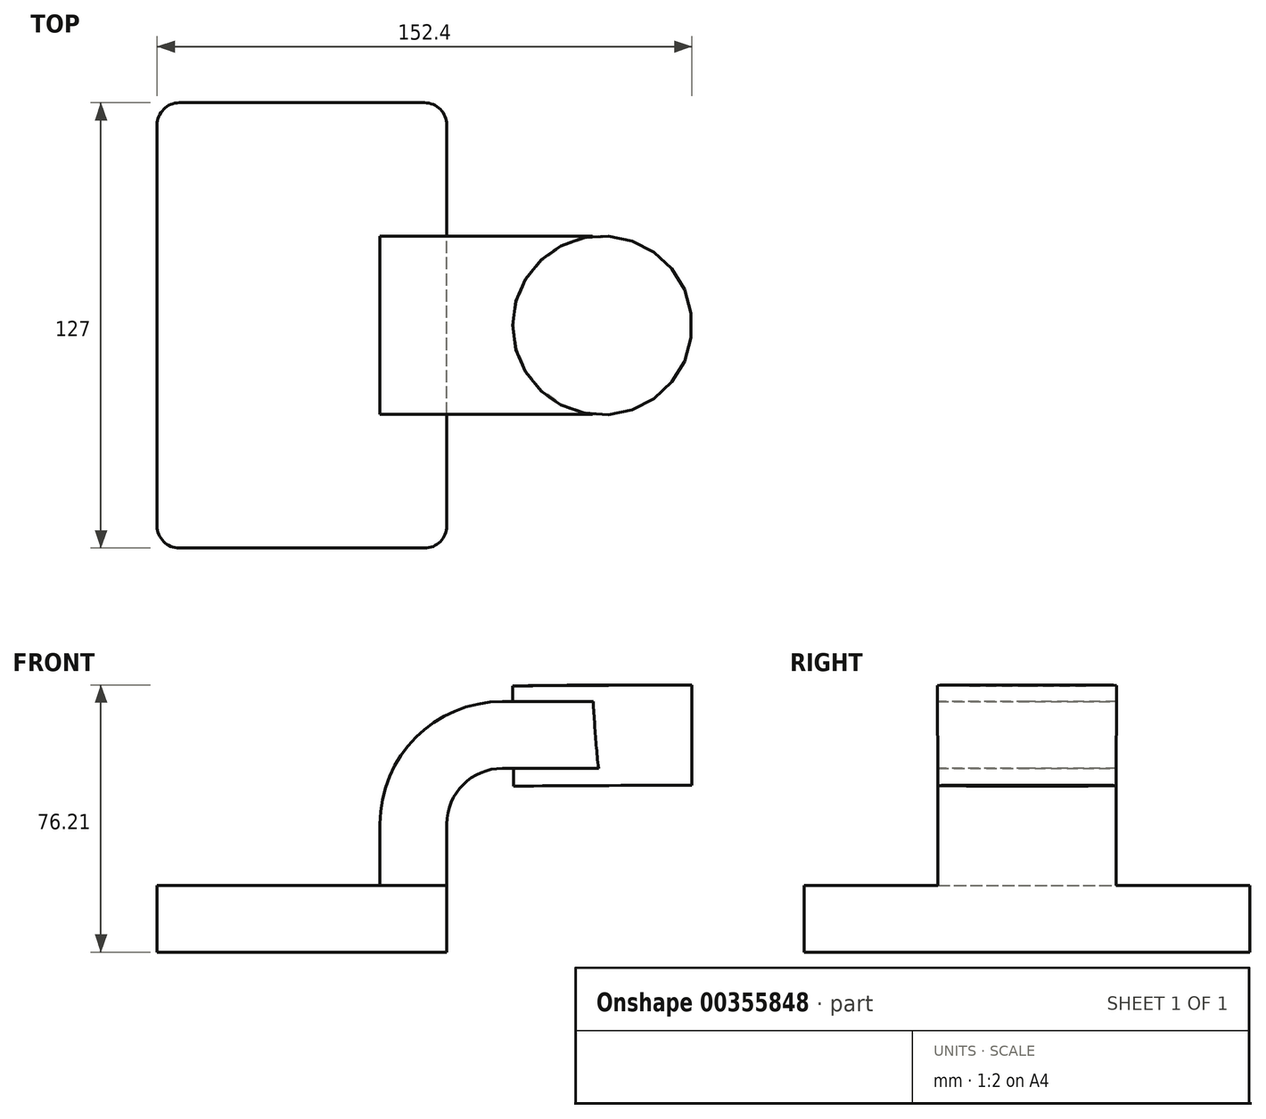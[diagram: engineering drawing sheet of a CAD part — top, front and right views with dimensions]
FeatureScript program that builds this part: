
annotation { "Feature Type Name" : "Feature", "Feature Type Description" : "" }
export const myFeature = defineFeature(function(context is Context, id is Id, definition is map)
    precondition{}
    {
        {
            var Q0;
            Q0=qCreatedBy(makeId("Front.planeOp"),FACE);
            var sketch = newSketch(context, id + "F0", { "sketchPlane" : qUnion([Q0])});
            skLineSegment(sketch, "E0.bottom", {"start": v(41.28, -9.52) * mm, "end": v(-41.28, -9.53) * mm});
            skLineSegment(sketch, "E0.top", {"start": v(41.28, 9.53) * mm, "end": v(-41.28, 9.53) * mm});
            skLineSegment(sketch, "E0.left", {"start": v(41.28, -9.52) * mm, "end": v(41.28, 9.53) * mm});
            skLineSegment(sketch, "E0.right", {"start": v(-41.28, -9.53) * mm, "end": v(-41.28, 9.53) * mm});
            skPoint(sketch, "E0.middle", {"position": v(0, 0) * mm});
            skLineSegment(sketch, "E1.bottom", {"start": v(111.12, 38.1) * mm, "end": v(60.32, 38.1) * mm});
            skLineSegment(sketch, "E1.top", {"start": v(111.12, 66.68) * mm, "end": v(60.32, 66.68) * mm});
            skLineSegment(sketch, "E1.left", {"start": v(111.12, 38.1) * mm, "end": v(111.12, 66.68) * mm});
            skLineSegment(sketch, "E1.right", {"start": v(60.32, 38.1) * mm, "end": v(60.32, 66.68) * mm});
            skPoint(sketch, "E1.middle", {"position": v(85.72, 52.39) * mm});
            skLineSegment(sketch, "E2", {"start": v(41.28, 9.53) * mm, "end": v(41.28, 27) * mm});
            skArc(sketch, "E3", {"start": v(41.27, 27) * mm, "mid": v(45.92, 38.23) * mm, "end": v(57.15, 42.88) * mm});
            skLineSegment(sketch, "E4", {"start": v(57.15, 42.88) * mm, "end": v(85.56, 42.88) * mm});
            skLineSegment(sketch, "E5.0", {"start": v(57.15, 61.93) * mm, "end": v(85.56, 61.93) * mm});
            skArc(sketch, "E5.1", {"start": v(22.23, 27) * mm, "mid": v(32.45, 51.7) * mm, "end": v(57.15, 61.93) * mm});
            skLineSegment(sketch, "E5.2", {"start": v(22.22, 9.53) * mm, "end": v(22.22, 27) * mm});
            skFitSpline(sketch, "E6", {"points": [v(-41.28, 9.52) * mm, v(57.15, 61.93) * mm], "startDerivative": vector(-2.62, 67.1) * mm, "endDerivative": vector(206.07, -1.73) * mm});
            skLineSegment(sketch, "E7", {"start": v(85.72, 38.1) * mm, "end": v(85.56, 66.68) * mm});
            skLineSegment(sketch, "E8", {"start": v(85.56, 61.93) * mm, "end": v(85.56, 42.88) * mm});
            skSolve(sketch);
        }
        {
            var Q0;
            Q0=makeQuery(id+"F0.imprint","IMPRINT",FACE,{"disambiguationData":[TD([[makeQuery(id+"F0.imprint","IMPRINT",EDGE,{"derivedFrom":sQuery(id+"F0.wireOp",EDGE,"E0.bottom")}),-1.0]])]});
            extrude(context, id + "F1", {"entities" : qUnion([Q0]), "endBound" : BoundingType.SYMMETRIC, "depth" : 127 * mm});
        }
        {
            var Q0;
            {var subQ0=sQuery(id+"F0.wireOp",EDGE,"E4");var subQ1=sQuery(id+"F0.wireOp",EDGE,"E1.right");var subQ2=makeQuery(id+"F0.imprint","INTERSECT",VERTEX,{"derivedFrom":[subQ1,subQ0]});Q0=makeQuery(id+"F0.imprint","IMPRINT",FACE,{"disambiguationData":[TD([[makeQuery(id+"F0.imprint","IMPRINT",EDGE,{"disambiguationData":[TD([[subQ2,-1.0]])],"derivedFrom":subQ1}),-1.0]])]});}
            var Q1;
            {var subQ1=sQuery(id+"F0.wireOp",EDGE,"E2");Q1=makeQuery(id+"F0.imprint","IMPRINT",FACE,{"disambiguationData":[TD([[makeQuery(id+"F0.imprint","IMPRINT",EDGE,{"derivedFrom":subQ1}),1.0]])]});}
            extrude(context, id + "F2", {"entities" : qUnion([Q0, Q1]), "operationType" : NewBodyOperationType.ADD, "endBound" : BoundingType.SYMMETRIC, "depth" : 50.8 * mm});
        }
        {
            var Q0;
            Q0=makeQuery(id+"F0.imprint","IMPRINT",FACE,{"disambiguationData":[TD([[makeQuery(id+"F0.imprint","IMPRINT",EDGE,{"derivedFrom":sQuery(id+"F0.wireOp",EDGE,"E5.1")}),1.0]])]});
            extrude(context, id + "F3", {"entities" : qUnion([Q0]), "operationType" : NewBodyOperationType.ADD, "endBound" : BoundingType.SYMMETRIC, "depth" : 15.88 * mm});
        }
        {
            var Q0;
            {var subQ0=sQuery(id+"F0.wireOp",EDGE,"E1.left");Q0=makeQuery(id+"F0.imprint","IMPRINT",FACE,{"disambiguationData":[TD([[makeQuery(id+"F0.imprint","IMPRINT",EDGE,{"derivedFrom":subQ0}),1.0]])]});}
            var Q1;
            Q1=sQuery(id+"F0.wireOp",EDGE,"E1.left");
            var Q2;
            Q2=sQuery(id+"F0.wireOp",EDGE,"E7");
            revolve(context, id + "F4", {"operationType" : NewBodyOperationType.ADD, "entities" : qUnion([Q0]), "surfaceEntities" : qUnion([Q1]), "axis" : qUnion([Q2]), "revolveType" : RevolveType.FULL});
        }
        {
            var Q0;
            Q0=makeQuery(id+"F1.opExtrude","CAP_EDGE",EDGE,{"disambiguationData":[OSD([sQuery(id+"F0.wireOp",EDGE,"E0.left")])],"isStart":true});
            var Q1;
            Q1=makeQuery(id+"F1.opExtrude","CAP_EDGE",EDGE,{"disambiguationData":[OSD([sQuery(id+"F0.wireOp",EDGE,"E0.right")])],"isStart":true});
            var Q2;
            Q2=makeQuery(id+"F1.opExtrude","CAP_EDGE",EDGE,{"disambiguationData":[OSD([sQuery(id+"F0.wireOp",EDGE,"E0.right")])],"isStart":false});
            var Q3;
            Q3=makeQuery(id+"F1.opExtrude","CAP_EDGE",EDGE,{"disambiguationData":[OSD([sQuery(id+"F0.wireOp",EDGE,"E0.left")])],"isStart":false});
            fillet(context, id + "F5", {"entities" : qUnion([Q0, Q1, Q2, Q3]), "radius" : 6.35 * mm, "tangentPropagation" : true, "allowEdgeOverflow" : false});
        }
    });
